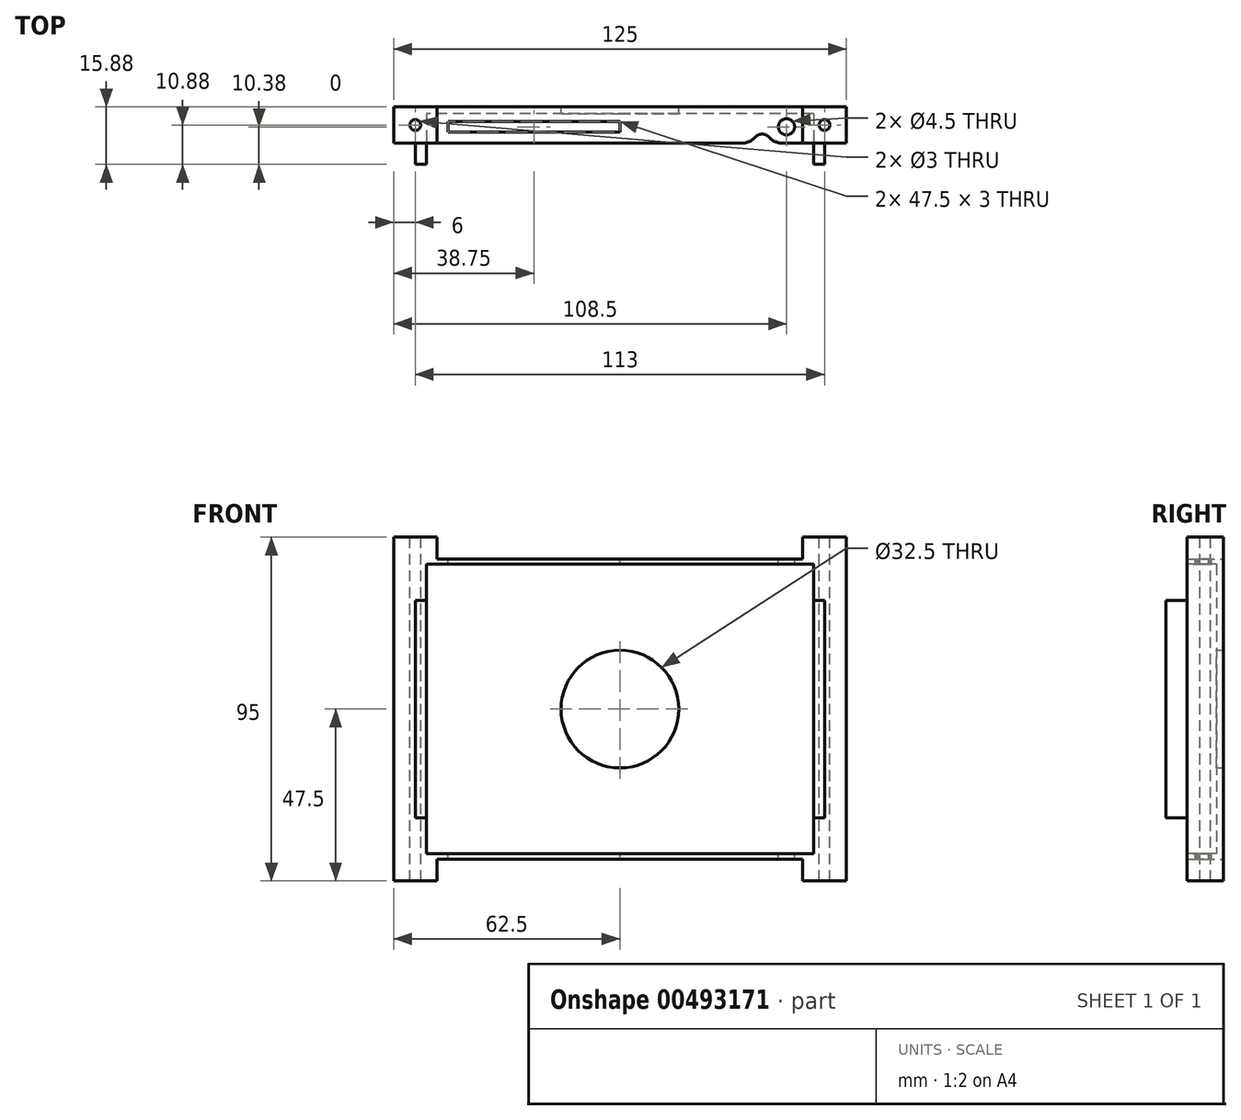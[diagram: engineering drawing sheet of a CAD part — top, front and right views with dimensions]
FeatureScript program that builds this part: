
annotation { "Feature Type Name" : "Feature", "Feature Type Description" : "" }
export const myFeature = defineFeature(function(context is Context, id is Id, definition is map)
    precondition{}
    {
        {
            var Q0;
            Q0=qCreatedBy(makeId("Front.planeOp"),FACE);
            var sketch = newSketch(context, id + "F0", { "sketchPlane" : qUnion([Q0])});
            skLineSegment(sketch, "E0.bottom", {"start": v(62.5, 47.5) * mm, "end": v(-62.5, 47.5) * mm, "construction": true});
            skLineSegment(sketch, "E0.top", {"start": v(62.5, -47.5) * mm, "end": v(-62.5, -47.5) * mm, "construction": true});
            skLineSegment(sketch, "E0.left", {"start": v(62.5, 47.5) * mm, "end": v(62.5, -47.5) * mm, "construction": true});
            skLineSegment(sketch, "E0.right", {"start": v(-62.5, 47.5) * mm, "end": v(-62.5, -47.5) * mm, "construction": true});
            skPoint(sketch, "E0.middle", {"position": v(0, 0) * mm});
            skLineSegment(sketch, "E1", {"start": v(-62.5, 47.5) * mm, "end": v(-50.5, 47.5) * mm});
            skLineSegment(sketch, "E2", {"start": v(62.5, 47.5) * mm, "end": v(50.5, 47.5) * mm});
            skLineSegment(sketch, "E3", {"start": v(50.5, 47.5) * mm, "end": v(50.5, 41.5) * mm});
            skLineSegment(sketch, "E4", {"start": v(50.5, 41.5) * mm, "end": v(-50.5, 41.5) * mm});
            skLineSegment(sketch, "E5", {"start": v(-50.5, 41.5) * mm, "end": v(-50.5, 47.5) * mm});
            skLineSegment(sketch, "E6", {"start": v(62.5, 47.5) * mm, "end": v(62.5, -47.5) * mm});
            skLineSegment(sketch, "E7", {"start": v(-62.5, -47.5) * mm, "end": v(-62.5, 47.5) * mm});
            skLineSegment(sketch, "E8", {"start": v(62.5, -47.5) * mm, "end": v(50.5, -47.5) * mm});
            skLineSegment(sketch, "E9", {"start": v(50.5, -47.5) * mm, "end": v(50.5, -41.5) * mm});
            skLineSegment(sketch, "E10", {"start": v(50.5, -41.5) * mm, "end": v(-50.5, -41.5) * mm});
            skLineSegment(sketch, "E11", {"start": v(-50.5, -41.5) * mm, "end": v(-50.5, -47.5) * mm});
            skLineSegment(sketch, "E12", {"start": v(-50.5, -47.5) * mm, "end": v(-62.5, -47.5) * mm});
            skCircle(sketch, "E13", {"center": v(0, 0) * mm, "radius": 16.25 * mm});
            skSolve(sketch);
        }
        {
            var Q0;
            Q0=qSketchRegion(id+"F0",true);
            extrude(context, id + "F1", {"entities" : qUnion([Q0]), "depth" : 15.88 * mm});
        }
        {
            var Q0;
            Q0=makeQuery(id+"F1.opExtrude","CAP_FACE",FACE,{"disambiguationData":[OSD([sQuery(id+"F0.wireOp",EDGE,"E1"),sQuery(id+"F0.wireOp",EDGE,"E2"),sQuery(id+"F0.wireOp",EDGE,"E3"),sQuery(id+"F0.wireOp",EDGE,"E4"),sQuery(id+"F0.wireOp",EDGE,"E5"),sQuery(id+"F0.wireOp",EDGE,"E6"),sQuery(id+"F0.wireOp",EDGE,"E7"),sQuery(id+"F0.wireOp",EDGE,"E8"),sQuery(id+"F0.wireOp",EDGE,"E9"),sQuery(id+"F0.wireOp",EDGE,"E10"),sQuery(id+"F0.wireOp",EDGE,"E11"),sQuery(id+"F0.wireOp",EDGE,"E12"),sQuery(id+"F0.wireOp",EDGE,"E13")])],"isStart":false});
            var sketch = newSketch(context, id + "F2", { "sketchPlane" : qUnion([Q0])});
            skLineSegment(sketch, "E14.bottom", {"start": v(56.5, 40) * mm, "end": v(-56.5, 40) * mm});
            skLineSegment(sketch, "E14.top", {"start": v(56.5, -40) * mm, "end": v(-56.5, -40) * mm});
            skLineSegment(sketch, "E14.left", {"start": v(56.5, 40) * mm, "end": v(56.5, -40) * mm});
            skLineSegment(sketch, "E14.right", {"start": v(-56.5, 40) * mm, "end": v(-56.5, -40) * mm});
            skPoint(sketch, "E14.middle", {"position": v(0, 0) * mm});
            skLineSegment(sketch, "E15.bottom", {"start": v(69.6, 57.77) * mm, "end": v(-69.6, 57.77) * mm});
            skLineSegment(sketch, "E15.top", {"start": v(69.6, -57.77) * mm, "end": v(-69.6, -57.77) * mm});
            skLineSegment(sketch, "E15.left", {"start": v(69.6, 57.77) * mm, "end": v(69.6, -57.77) * mm});
            skLineSegment(sketch, "E15.right", {"start": v(-69.6, 57.77) * mm, "end": v(-69.6, -57.77) * mm});
            skSolve(sketch);
        }
        {
            var Q0;
            Q0 = qSketchRegion(id + "F2", true);
            extrude(context, id + "F3", {"entities" : qUnion([Q0]), "operationType" : NewBodyOperationType.REMOVE, "oppositeDirection" : true, "depth" : 5.88 * mm});
        }
        {
            var Q0;
            Q0=makeQuery(id+"F1.opExtrude","CAP_FACE",FACE,{"disambiguationData":[OSD([sQuery(id+"F0.wireOp",EDGE,"E1"),sQuery(id+"F0.wireOp",EDGE,"E2"),sQuery(id+"F0.wireOp",EDGE,"E3"),sQuery(id+"F0.wireOp",EDGE,"E4"),sQuery(id+"F0.wireOp",EDGE,"E5"),sQuery(id+"F0.wireOp",EDGE,"E6"),sQuery(id+"F0.wireOp",EDGE,"E7"),sQuery(id+"F0.wireOp",EDGE,"E8"),sQuery(id+"F0.wireOp",EDGE,"E9"),sQuery(id+"F0.wireOp",EDGE,"E10"),sQuery(id+"F0.wireOp",EDGE,"E11"),sQuery(id+"F0.wireOp",EDGE,"E12"),sQuery(id+"F0.wireOp",EDGE,"E13")])],"isStart":false});
            var sketch = newSketch(context, id + "F4", { "sketchPlane" : qUnion([Q0])});
            skLineSegment(sketch, "E16.bottom", {"start": v(53.5, 40) * mm, "end": v(-53.5, 40) * mm});
            skLineSegment(sketch, "E16.top", {"start": v(53.5, -40) * mm, "end": v(-53.5, -40) * mm});
            skLineSegment(sketch, "E16.left", {"start": v(53.5, 40) * mm, "end": v(53.5, -40) * mm});
            skLineSegment(sketch, "E16.right", {"start": v(-53.5, 40) * mm, "end": v(-53.5, -40) * mm});
            skPoint(sketch, "E16.middle", {"position": v(0, 0) * mm});
            skSolve(sketch);
        }
        {
            var Q0;
            Q0 = qSketchRegion(id + "F4", true);
            extrude(context, id + "F5", {"entities" : qUnion([Q0]), "operationType" : NewBodyOperationType.REMOVE, "oppositeDirection" : true, "depth" : 14 * mm});
        }
        {
            var Q0;
            Q0=makeQuery(id+"F5.boolean.opBoolean","SPLIT",FACE,{"disambiguationData":[TD([makeQuery(id+"F3.boolean.opBoolean","COPY",FACE,{"derivedFrom":makeQuery(id+"F3.opExtrude","SWEPT_FACE",FACE,{"disambiguationData":[OSD([sQuery(id+"F2.wireOp",EDGE,"E14.right")])]})})])],"derivedFrom":makeQuery(id+"F1.opExtrude","CAP_FACE",FACE,{"disambiguationData":[OSD([sQuery(id+"F0.wireOp",EDGE,"E1"),sQuery(id+"F0.wireOp",EDGE,"E2"),sQuery(id+"F0.wireOp",EDGE,"E3"),sQuery(id+"F0.wireOp",EDGE,"E4"),sQuery(id+"F0.wireOp",EDGE,"E5"),sQuery(id+"F0.wireOp",EDGE,"E6"),sQuery(id+"F0.wireOp",EDGE,"E7"),sQuery(id+"F0.wireOp",EDGE,"E8"),sQuery(id+"F0.wireOp",EDGE,"E9"),sQuery(id+"F0.wireOp",EDGE,"E10"),sQuery(id+"F0.wireOp",EDGE,"E11"),sQuery(id+"F0.wireOp",EDGE,"E12"),sQuery(id+"F0.wireOp",EDGE,"E13")])],"isStart":false})});
            var sketch = newSketch(context, id + "F6", { "sketchPlane" : qUnion([Q0])});
            skLineSegment(sketch, "E17.bottom", {"start": v(-60.23, 43.15) * mm, "end": v(60.36, 43.15) * mm});
            skLineSegment(sketch, "E17.top", {"start": v(-60.23, 30) * mm, "end": v(60.36, 30) * mm});
            skLineSegment(sketch, "E17.left", {"start": v(-60.23, 43.15) * mm, "end": v(-60.23, 30) * mm});
            skLineSegment(sketch, "E17.right", {"start": v(60.36, 43.15) * mm, "end": v(60.36, 30) * mm});
            skLineSegment(sketch, "E18.bottom", {"start": v(-59.64, -45.81) * mm, "end": v(61.69, -45.81) * mm});
            skLineSegment(sketch, "E18.top", {"start": v(-59.64, -30) * mm, "end": v(61.69, -30) * mm});
            skLineSegment(sketch, "E18.left", {"start": v(-59.64, -45.81) * mm, "end": v(-59.64, -30) * mm});
            skLineSegment(sketch, "E18.right", {"start": v(61.69, -45.81) * mm, "end": v(61.69, -30) * mm});
            skSolve(sketch);
        }
        {
            var Q0;
            Q0 = qSketchRegion(id + "F6", true);
            extrude(context, id + "F7", {"entities" : qUnion([Q0]), "operationType" : NewBodyOperationType.REMOVE, "oppositeDirection" : true, "depth" : 5.88 * mm});
        }
        {
            var Q0;
            Q0=makeQuery(id+"F1.opExtrude","SWEPT_FACE",FACE,{"disambiguationData":[OSD([sQuery(id+"F0.wireOp",EDGE,"E4")])]});
            var sketch = newSketch(context, id + "F8", { "sketchPlane" : qUnion([Q0])});
            skCircle(sketch, "E19", {"center": v(46, -5.5) * mm, "radius": 1.5 * mm});
            skLineSegment(sketch, "E20.bottom", {"start": v(41.5, -4) * mm, "end": v(-47.5, -4) * mm});
            skLineSegment(sketch, "E20.top", {"start": v(41.5, -7) * mm, "end": v(-47.5, -7) * mm});
            skLineSegment(sketch, "E20.left", {"start": v(41.5, -4) * mm, "end": v(41.5, -7) * mm});
            skLineSegment(sketch, "E20.right", {"start": v(-47.5, -4) * mm, "end": v(-47.5, -7) * mm});
            skSolve(sketch);
        }
        {
            var Q0;
            Q0 = qSketchRegion(id + "F8", true);
            extrude(context, id + "F9", {"entities" : qUnion([Q0]), "operationType" : NewBodyOperationType.REMOVE, "oppositeDirection" : true, "depth" : 100 * mm});
        }
        {
            var Q0;
            Q0=makeQuery(id+"F1.opExtrude","SWEPT_FACE",FACE,{"disambiguationData":[OSD([sQuery(id+"F0.wireOp",EDGE,"E4")])]});
            var sketch = newSketch(context, id + "F10", { "sketchPlane" : qUnion([Q0])});
            skLineSegment(sketch, "E21.bottom", {"start": v(0, 0) * mm, "end": v(42.44, 0) * mm});
            skLineSegment(sketch, "E21.top", {"start": v(0, -10) * mm, "end": v(42.44, -10) * mm});
            skLineSegment(sketch, "E21.left", {"start": v(0, 0) * mm, "end": v(0, -10) * mm});
            skLineSegment(sketch, "E21.right", {"start": v(42.44, 0) * mm, "end": v(42.44, -10) * mm});
            skSolve(sketch);
        }
        {
            var Q0;
            Q0 = qSketchRegion(id + "F10", true);
            extrude(context, id + "F11", {"entities" : qUnion([Q0]), "operationType" : NewBodyOperationType.ADD, "oppositeDirection" : true, "depth" : 1.5 * mm});
        }
        {
            var Q0;
            Q0=makeQuery(id+"F1.opExtrude","SWEPT_FACE",FACE,{"disambiguationData":[OSD([sQuery(id+"F0.wireOp",EDGE,"E10")])]});
            var sketch = newSketch(context, id + "F12", { "sketchPlane" : qUnion([Q0])});
            skLineSegment(sketch, "E22.bottom", {"start": v(0, 10) * mm, "end": v(42.52, 10) * mm});
            skLineSegment(sketch, "E22.top", {"start": v(0, 0) * mm, "end": v(42.52, 0) * mm});
            skLineSegment(sketch, "E22.left", {"start": v(0, 10) * mm, "end": v(0, 0) * mm});
            skLineSegment(sketch, "E22.right", {"start": v(42.52, 10) * mm, "end": v(42.52, 0) * mm});
            skSolve(sketch);
        }
        {
            var Q0;
            Q0 = qSketchRegion(id + "F12", true);
            extrude(context, id + "F13", {"entities" : qUnion([Q0]), "operationType" : NewBodyOperationType.ADD, "oppositeDirection" : true, "depth" : 1.5 * mm});
        }
        {
            var Q0;
            Q0=makeQuery(id+"F13.boolean.opBoolean","MERGE",FACE,{"derivedFrom":[makeQuery(id+"F1.opExtrude","SWEPT_FACE",FACE,{"disambiguationData":[OSD([sQuery(id+"F0.wireOp",EDGE,"E10")])]}),makeQuery(id+"F13.opExtrude","CAP_FACE",FACE,{"disambiguationData":[OSD([sQuery(id+"F12.wireOp",EDGE,"E22.bottom"),sQuery(id+"F12.wireOp",EDGE,"E22.top"),sQuery(id+"F12.wireOp",EDGE,"E22.left"),sQuery(id+"F12.wireOp",EDGE,"E22.right")])],"isStart":true})]});
            var sketch = newSketch(context, id + "F14", { "sketchPlane" : qUnion([Q0])});
            skCircle(sketch, "E23", {"center": v(39.25, 10) * mm, "radius": 2.5 * mm});
            skSolve(sketch);
        }
        {
            var Q0;
            Q0 = qSketchRegion(id + "F14", true);
            extrude(context, id + "F15", {"entities" : qUnion([Q0]), "operationType" : NewBodyOperationType.REMOVE, "oppositeDirection" : true, "depth" : 95.5 * mm});
        }
        {
            var Q0;
            Q0=makeQuery(id+"F11.boolean.opBoolean","MERGE",FACE,{"derivedFrom":[makeQuery(id+"F1.opExtrude","SWEPT_FACE",FACE,{"disambiguationData":[OSD([sQuery(id+"F0.wireOp",EDGE,"E4")])]}),makeQuery(id+"F11.opExtrude","CAP_FACE",FACE,{"disambiguationData":[OSD([sQuery(id+"F10.wireOp",EDGE,"E21.bottom"),sQuery(id+"F10.wireOp",EDGE,"E21.top"),sQuery(id+"F10.wireOp",EDGE,"E21.left"),sQuery(id+"F10.wireOp",EDGE,"E21.right")])],"isStart":true})]});
            var sketch = newSketch(context, id + "F16", { "sketchPlane" : qUnion([Q0])});
            skCircle(sketch, "E24", {"center": v(46, -5.5) * mm, "radius": 2.25 * mm});
            skSolve(sketch);
        }
        {
            var Q0;
            Q0 = qSketchRegion(id + "F16", true);
            extrude(context, id + "F17", {"entities" : qUnion([Q0]), "operationType" : NewBodyOperationType.REMOVE, "oppositeDirection" : true, "depth" : 200 * mm});
        }
        {
            var Q0;
            Q0=makeQuery(id+"F15.boolean.opBoolean","INTERSECT",EDGE,{"disambiguationData":[OD(3.0)],"derivedFrom":[makeQuery(id+"F7.boolean.opBoolean","MERGE",FACE,{"derivedFrom":[makeQuery(id+"F3.boolean.opBoolean","COPY",FACE,{"derivedFrom":makeQuery(id+"F3.opExtrude","CAP_FACE",FACE,{"disambiguationData":[OSD([sQuery(id+"F2.wireOp",EDGE,"E14.bottom"),sQuery(id+"F2.wireOp",EDGE,"E14.top"),sQuery(id+"F2.wireOp",EDGE,"E14.left"),sQuery(id+"F2.wireOp",EDGE,"E14.right"),sQuery(id+"F2.wireOp",EDGE,"E15.bottom"),sQuery(id+"F2.wireOp",EDGE,"E15.top"),sQuery(id+"F2.wireOp",EDGE,"E15.left"),sQuery(id+"F2.wireOp",EDGE,"E15.right")])],"isStart":false})}),makeQuery(id+"F7.opExtrude","CAP_FACE",FACE,{"disambiguationData":[OSD([sQuery(id+"F6.wireOp",EDGE,"E17.bottom"),sQuery(id+"F6.wireOp",EDGE,"E17.top"),sQuery(id+"F6.wireOp",EDGE,"E17.left"),sQuery(id+"F6.wireOp",EDGE,"E17.right")])],"isStart":false}),makeQuery(id+"F7.opExtrude","CAP_FACE",FACE,{"disambiguationData":[OSD([sQuery(id+"F6.wireOp",EDGE,"E18.bottom"),sQuery(id+"F6.wireOp",EDGE,"E18.top"),sQuery(id+"F6.wireOp",EDGE,"E18.left"),sQuery(id+"F6.wireOp",EDGE,"E18.right")])],"isStart":false})]}),makeQuery(id+"F15.opExtrude","SWEPT_FACE",FACE,{"disambiguationData":[OSD([sQuery(id+"F14.wireOp",EDGE,"E23")])]})]});
            var Q1;
            Q1=makeQuery(id+"F15.boolean.opBoolean","INTERSECT",EDGE,{"disambiguationData":[OD(2.0)],"derivedFrom":[makeQuery(id+"F7.boolean.opBoolean","MERGE",FACE,{"derivedFrom":[makeQuery(id+"F3.boolean.opBoolean","COPY",FACE,{"derivedFrom":makeQuery(id+"F3.opExtrude","CAP_FACE",FACE,{"disambiguationData":[OSD([sQuery(id+"F2.wireOp",EDGE,"E14.bottom"),sQuery(id+"F2.wireOp",EDGE,"E14.top"),sQuery(id+"F2.wireOp",EDGE,"E14.left"),sQuery(id+"F2.wireOp",EDGE,"E14.right"),sQuery(id+"F2.wireOp",EDGE,"E15.bottom"),sQuery(id+"F2.wireOp",EDGE,"E15.top"),sQuery(id+"F2.wireOp",EDGE,"E15.left"),sQuery(id+"F2.wireOp",EDGE,"E15.right")])],"isStart":false})}),makeQuery(id+"F7.opExtrude","CAP_FACE",FACE,{"disambiguationData":[OSD([sQuery(id+"F6.wireOp",EDGE,"E17.bottom"),sQuery(id+"F6.wireOp",EDGE,"E17.top"),sQuery(id+"F6.wireOp",EDGE,"E17.left"),sQuery(id+"F6.wireOp",EDGE,"E17.right")])],"isStart":false}),makeQuery(id+"F7.opExtrude","CAP_FACE",FACE,{"disambiguationData":[OSD([sQuery(id+"F6.wireOp",EDGE,"E18.bottom"),sQuery(id+"F6.wireOp",EDGE,"E18.top"),sQuery(id+"F6.wireOp",EDGE,"E18.left"),sQuery(id+"F6.wireOp",EDGE,"E18.right")])],"isStart":false})]}),makeQuery(id+"F15.opExtrude","SWEPT_FACE",FACE,{"disambiguationData":[OSD([sQuery(id+"F14.wireOp",EDGE,"E23")])]})]});
            fillet(context, id + "F18", {"entities" : qUnion([Q0, Q1]), "radius" : 5 * mm, "tangentPropagation" : true, "allowEdgeOverflow" : false});
        }
        {
            var Q0;
            Q0=makeQuery(id+"F1.opExtrude","SWEPT_FACE",FACE,{"disambiguationData":[OSD([sQuery(id+"F0.wireOp",EDGE,"E1")])]});
            var sketch = newSketch(context, id + "F19", { "sketchPlane" : qUnion([Q0])});
            skLineSegment(sketch, "E25", {"start": v(-62.5, -10) * mm, "end": v(-50.5, 0) * mm, "construction": true});
            skCircle(sketch, "E26", {"center": v(-56.5, -5) * mm, "radius": 1.5 * mm});
            skSolve(sketch);
        }
        {
            var Q0;
            Q0 = qSketchRegion(id + "F19", true);
            extrude(context, id + "F20", {"entities" : qUnion([Q0]), "operationType" : NewBodyOperationType.REMOVE, "oppositeDirection" : true, "depth" : 106.2 * mm});
        }
        {
            var Q0;
            Q0=makeQuery(id+"F1.opExtrude","SWEPT_FACE",FACE,{"disambiguationData":[OSD([sQuery(id+"F0.wireOp",EDGE,"E2")])]});
            var sketch = newSketch(context, id + "F21", { "sketchPlane" : qUnion([Q0])});
            skLineSegment(sketch, "E27", {"start": v(62.5, 0) * mm, "end": v(50.5, -10) * mm, "construction": true});
            skCircle(sketch, "E28", {"center": v(56.5, -5) * mm, "radius": 1.5 * mm});
            skSolve(sketch);
        }
        {
            var Q0;
            Q0 = qSketchRegion(id + "F21", true);
            extrude(context, id + "F22", {"entities" : qUnion([Q0]), "operationType" : NewBodyOperationType.REMOVE, "oppositeDirection" : true, "depth" : 121.8 * mm});
        }
    });
